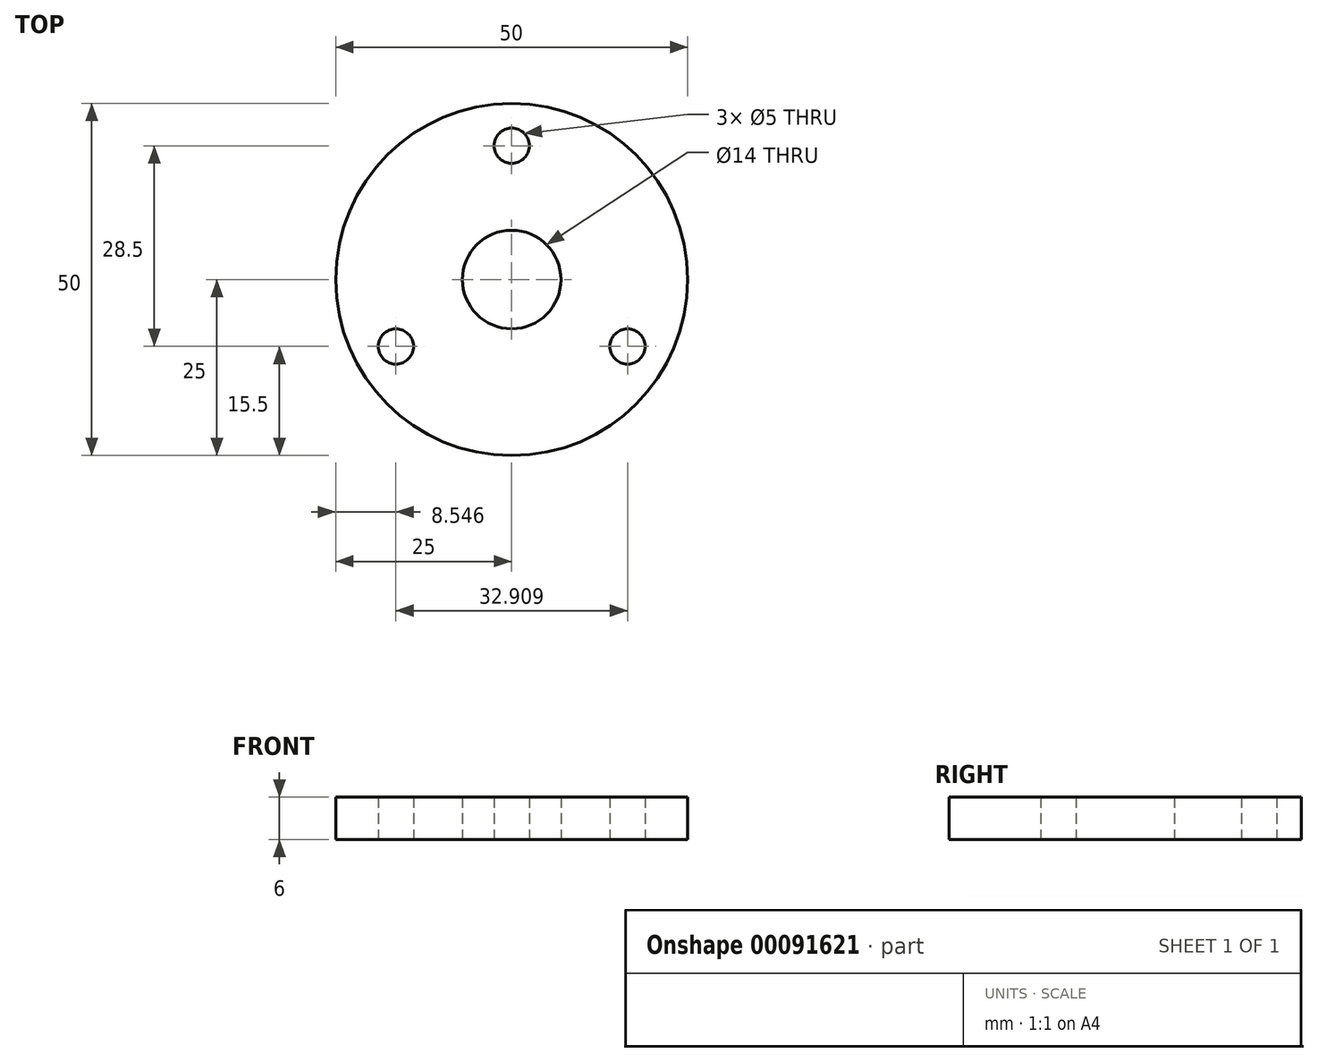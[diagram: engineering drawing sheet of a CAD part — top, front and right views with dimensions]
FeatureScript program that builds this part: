
annotation { "Feature Type Name" : "Feature", "Feature Type Description" : "" }
export const myFeature = defineFeature(function(context is Context, id is Id, definition is map)
    precondition{}
    {
        {
            var Q0;
            Q0=qCreatedBy(makeId("Top.planeOp"),FACE);
            var sketch = newSketch(context, id + "F0", { "sketchPlane" : qUnion([Q0])});
            skCircle(sketch, "E0", {"center": v(0, 0) * mm, "radius": 7 * mm});
            skCircle(sketch, "E1", {"center": v(0, 0) * mm, "radius": 25 * mm});
            skCircle(sketch, "E2", {"center": v(0, 19) * mm, "radius": 2.5 * mm});
            skCircle(sketch, "E3.1.0", {"center": v(-16.45, -9.5) * mm, "radius": 2.5 * mm});
            skCircle(sketch, "E3.2.0", {"center": v(16.45, -9.5) * mm, "radius": 2.5 * mm});
            skLineSegment(sketch, "E4", {"start": v(0, 0) * mm, "end": v(16.45, -9.5) * mm, "construction": true});
            skLineSegment(sketch, "E5", {"start": v(0, 0) * mm, "end": v(-16.45, -9.5) * mm, "construction": true});
            skSolve(sketch);
        }
        {
            var Q0;
            Q0=makeQuery(id+"F0.imprint","IMPRINT",FACE,{"disambiguationData":[TD([[makeQuery(id+"F0.imprint","IMPRINT",EDGE,{"derivedFrom":sQuery(id+"F0.wireOp",EDGE,"E0")}),-1.0]])]});
            extrude(context, id + "F1", {"entities" : qUnion([Q0]), "depth" : 6 * mm});
        }
    });
